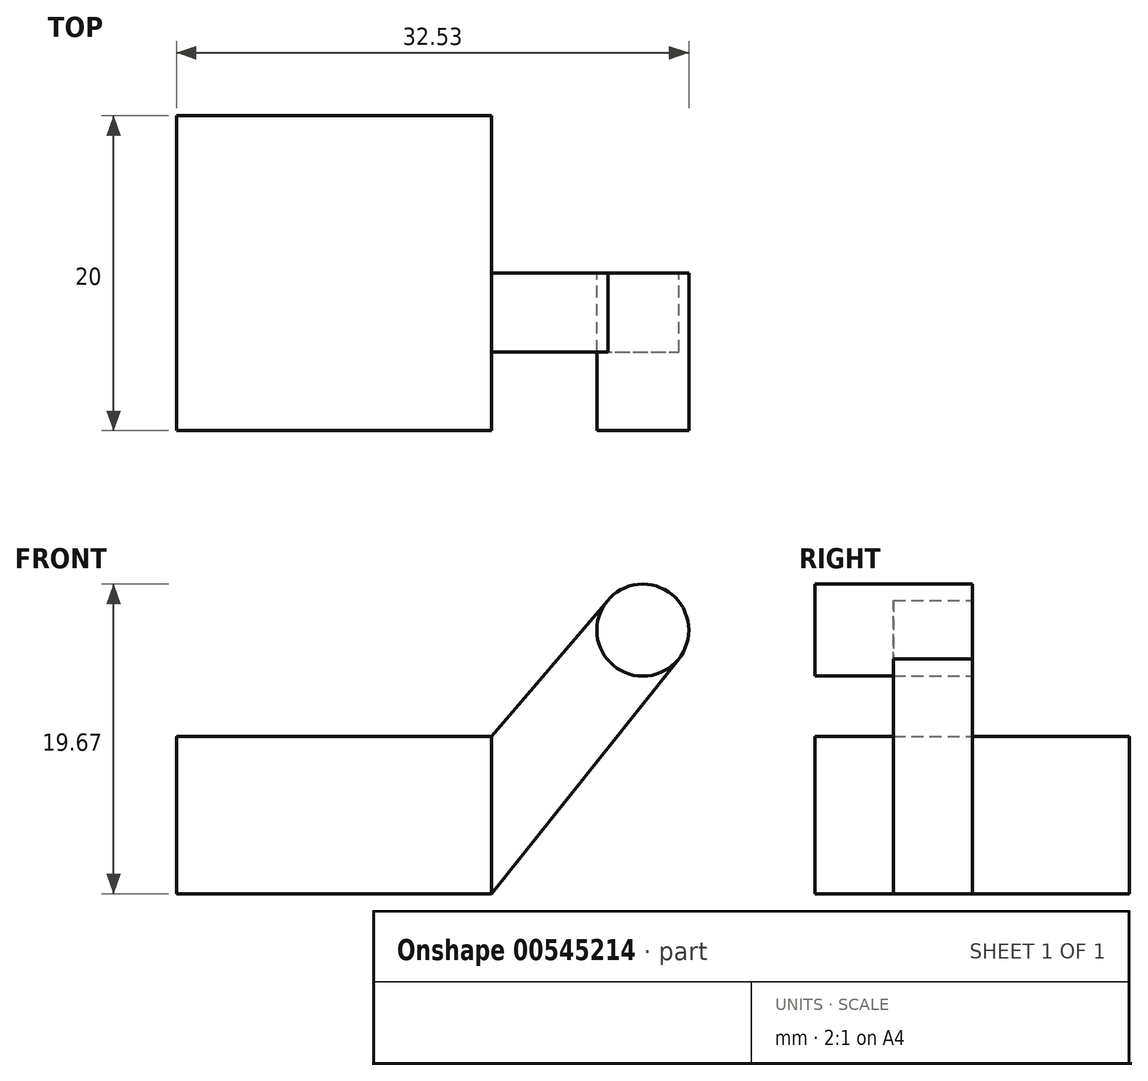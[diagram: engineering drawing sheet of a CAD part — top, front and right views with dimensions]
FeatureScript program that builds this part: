
annotation { "Feature Type Name" : "Feature", "Feature Type Description" : "" }
export const myFeature = defineFeature(function(context is Context, id is Id, definition is map)
    precondition{}
    {
        {
            var Q0;
            Q0=qCreatedBy(makeId("Front.planeOp"),FACE);
            var sketch = newSketch(context, id + "F0", { "sketchPlane" : qUnion([Q0])});
            skLineSegment(sketch, "E0.bottom", {"start": v(-29.61, 0) * mm, "end": v(-9.61, 0) * mm});
            skLineSegment(sketch, "E0.top", {"start": v(-29.61, 10) * mm, "end": v(-9.61, 10) * mm});
            skLineSegment(sketch, "E0.left", {"start": v(-29.61, 0) * mm, "end": v(-29.61, 10) * mm});
            skLineSegment(sketch, "E0.right", {"start": v(-9.61, 0) * mm, "end": v(-9.61, 10) * mm});
            skPoint(sketch, "E1.orphan", {"position": v(0, 10) * mm});
            skCircle(sketch, "E2", {"center": v(0, 16.75) * mm, "radius": 2.92 * mm});
            skLineSegment(sketch, "E3", {"start": v(-9.61, 10) * mm, "end": v(-2.22, 18.64) * mm});
            skLineSegment(sketch, "E4", {"start": v(-9.61, 0) * mm, "end": v(2.29, 14.92) * mm});
            skSolve(sketch);
        }
        {
            var Q0;
            {var subQ0=sQuery(id+"F0.wireOp",EDGE,"E2");var subQ1=makeQuery(id+"F0.imprint","INTERSECT",VERTEX,{"derivedFrom":[subQ0,sQuery(id+"F0.wireOp",EDGE,"E3")]});Q0=makeQuery(id+"F0.imprint","IMPRINT",FACE,{"disambiguationData":[TD([[makeQuery(id+"F0.imprint","IMPRINT",EDGE,{"disambiguationData":[TD([[subQ1,-1.0]])],"derivedFrom":subQ0}),1.0]])]});}
            var Q1;
            Q1=makeQuery(id+"F0.imprint","IMPRINT",FACE,{"disambiguationData":[TD([[makeQuery(id+"F0.imprint","IMPRINT",EDGE,{"derivedFrom":sQuery(id+"F0.wireOp",EDGE,"E0.bottom")}),1.0]])]});
            extrude(context, id + "F1", {"entities" : qUnion([Q0, Q1]), "depth" : 10 * mm, "offsetDistance" : 25 * mm});
        }
        {
            var Q0;
            Q0=makeQuery(id+"F0.imprint","IMPRINT",FACE,{"disambiguationData":[TD([[makeQuery(id+"F0.imprint","IMPRINT",EDGE,{"derivedFrom":sQuery(id+"F0.wireOp",EDGE,"E0.right")}),-1.0]])]});
            extrude(context, id + "F2", {"entities" : qUnion([Q0]), "depth" : 5 * mm, "offsetDistance" : 25 * mm});
        }
        {
            var Q0;
            Q0=makeQuery(id+"F1.opExtrude","SWEPT_BODY",BODY,{"disambiguationData":[OSD([sQuery(id+"F0.wireOp",EDGE,"E0.bottom"),sQuery(id+"F0.wireOp",EDGE,"E0.top"),sQuery(id+"F0.wireOp",EDGE,"E0.left"),sQuery(id+"F0.wireOp",EDGE,"E0.right")])]});
            var Q1;
            Q1=qCreatedBy(makeId("Front.planeOp"),FACE);
            mirror(context, id + "F3", {"operationType" : NewBodyOperationType.ADD, "entities" : qUnion([Q0]), "mirrorPlane" : qUnion([Q1])});
        }
    });
